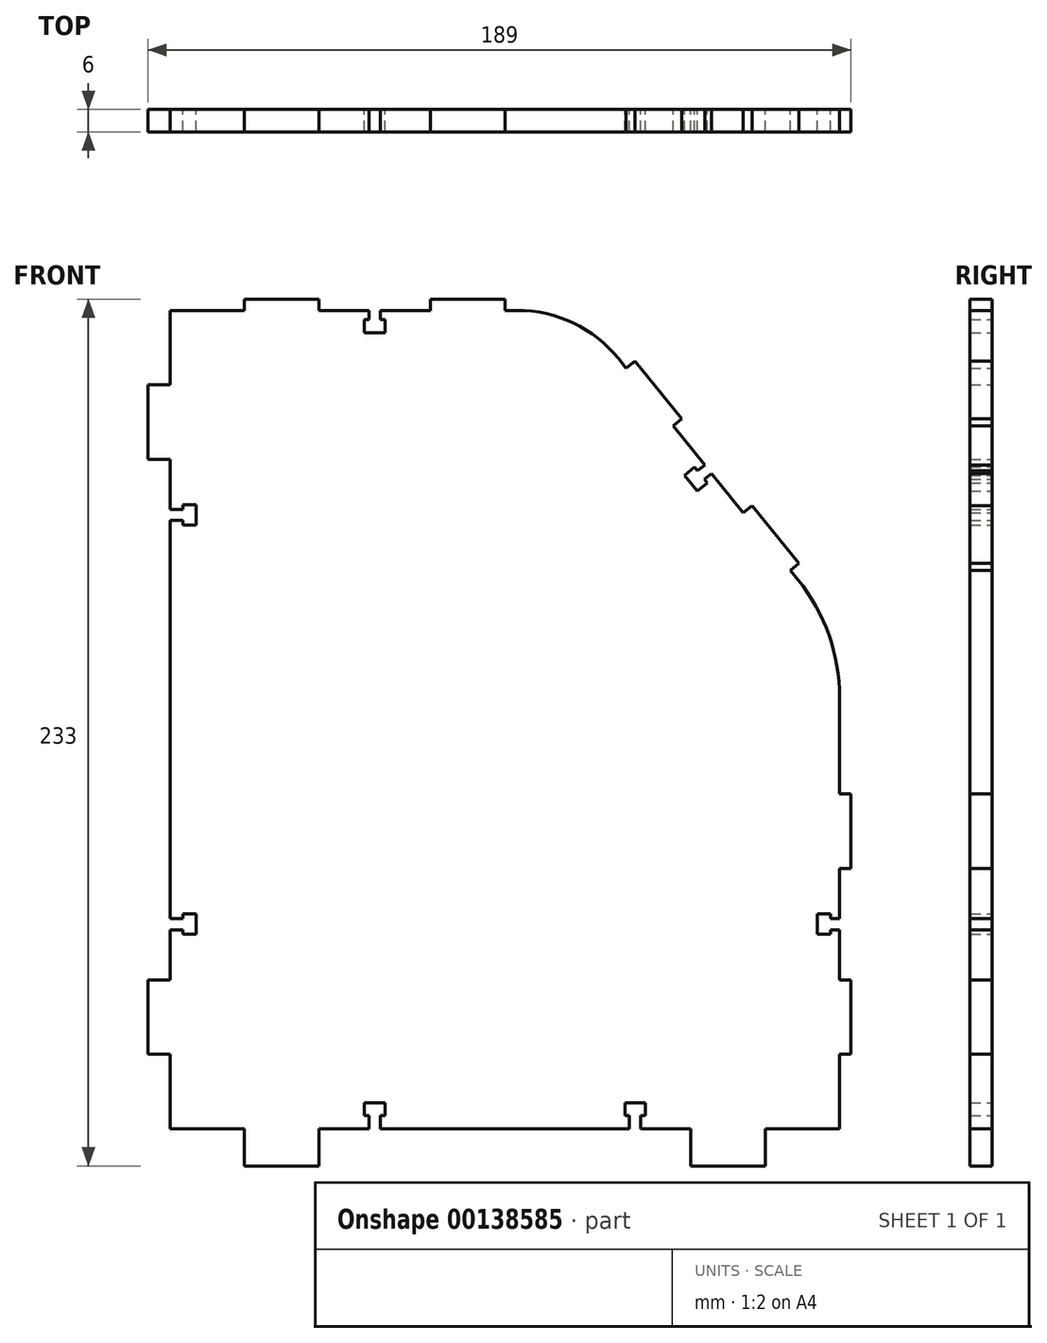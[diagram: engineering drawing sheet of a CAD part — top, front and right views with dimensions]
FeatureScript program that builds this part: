
annotation { "Feature Type Name" : "Feature", "Feature Type Description" : "" }
export const myFeature = defineFeature(function(context is Context, id is Id, definition is map)
    precondition{}
    {
        {
            var Q0;
            Q0=qCreatedBy(makeId("Front.planeOp"),FACE);
            var sketch = newSketch(context, id + "F0", { "sketchPlane" : qUnion([Q0])});
            skLineSegment(sketch, "E0", {"start": v(0, 220) * mm, "end": v(20, 220) * mm});
            skLineSegment(sketch, "E1", {"start": v(20, 220) * mm, "end": v(20, 223) * mm});
            skLineSegment(sketch, "E2", {"start": v(20, 223) * mm, "end": v(40, 223) * mm});
            skLineSegment(sketch, "E3", {"start": v(40, 223) * mm, "end": v(40, 220) * mm});
            skLineSegment(sketch, "E4", {"start": v(40, 220) * mm, "end": v(53.5, 220) * mm});
            skLineSegment(sketch, "E5", {"start": v(53.5, 220) * mm, "end": v(53.5, 217.5) * mm});
            skLineSegment(sketch, "E6", {"start": v(53.5, 217.5) * mm, "end": v(52.25, 217.5) * mm});
            skLineSegment(sketch, "E7", {"start": v(52.25, 217.5) * mm, "end": v(52.25, 214) * mm});
            skLineSegment(sketch, "E8", {"start": v(52.25, 214) * mm, "end": v(57.75, 214) * mm});
            skLineSegment(sketch, "E9", {"start": v(57.75, 214) * mm, "end": v(57.75, 217.5) * mm});
            skLineSegment(sketch, "E10", {"start": v(57.75, 217.5) * mm, "end": v(56.5, 217.5) * mm});
            skLineSegment(sketch, "E11", {"start": v(56.5, 217.5) * mm, "end": v(56.5, 220) * mm});
            skLineSegment(sketch, "E12", {"start": v(56.5, 220) * mm, "end": v(70, 220) * mm});
            skLineSegment(sketch, "E13", {"start": v(70, 220) * mm, "end": v(70, 223) * mm});
            skLineSegment(sketch, "E14", {"start": v(70, 223) * mm, "end": v(90, 223) * mm});
            skLineSegment(sketch, "E15", {"start": v(90, 223) * mm, "end": v(90, 220) * mm});
            skLineSegment(sketch, "E16", {"start": v(90, 220) * mm, "end": v(93.33, 220) * mm});
            skLineSegment(sketch, "E17", {"start": v(0, 200) * mm, "end": v(-6, 200) * mm});
            skLineSegment(sketch, "E18", {"start": v(-6, 200) * mm, "end": v(-6, 180) * mm});
            skLineSegment(sketch, "E19", {"start": v(-6, 180) * mm, "end": v(0, 180) * mm});
            skLineSegment(sketch, "E20", {"start": v(0, 166.5) * mm, "end": v(3.5, 166.5) * mm});
            skLineSegment(sketch, "E21", {"start": v(3.5, 166.5) * mm, "end": v(3.5, 167.75) * mm});
            skLineSegment(sketch, "E22", {"start": v(3.5, 167.75) * mm, "end": v(7, 167.75) * mm});
            skLineSegment(sketch, "E23", {"start": v(7, 167.75) * mm, "end": v(7, 162.25) * mm});
            skLineSegment(sketch, "E24", {"start": v(7, 162.25) * mm, "end": v(3.5, 162.25) * mm});
            skLineSegment(sketch, "E25", {"start": v(3.5, 162.25) * mm, "end": v(3.5, 163.5) * mm});
            skLineSegment(sketch, "E26", {"start": v(3.5, 163.5) * mm, "end": v(0, 163.5) * mm});
            skLineSegment(sketch, "E27", {"start": v(0, 166.5) * mm, "end": v(0, 180) * mm});
            skLineSegment(sketch, "E28", {"start": v(-6, 180) * mm, "end": v(-6, 200) * mm});
            skLineSegment(sketch, "E29", {"start": v(0, 200) * mm, "end": v(0, 220) * mm});
            skPoint(sketch, "E30.visualSharp", {"position": v(110, 220) * mm});
            skArc(sketch, "E30.filletArc", {"start": v(120.5, 207.06) * mm, "mid": v(108.38, 216.6) * mm, "end": v(93.33, 220) * mm});
            skPoint(sketch, "E31.visualSharp", {"position": v(180, 135.15) * mm});
            skArc(sketch, "E31.filletArc", {"start": v(180, 116.03) * mm, "mid": v(177.12, 132.74) * mm, "end": v(168.82, 147.54) * mm});
            skLineSegment(sketch, "E32", {"start": v(0, 163.5) * mm, "end": v(0, 110) * mm});
            skLineSegment(sketch, "E33.MirrorCS", {"start": v(0, 0) * mm, "end": v(0, 0) * mm});
            skLineSegment(sketch, "E34", {"start": v(93.33, 185) * mm, "end": v(110, 220.02) * mm});
            skLineSegment(sketch, "E35", {"start": v(0, 110) * mm, "end": v(180, 110) * mm, "construction": true});
            skLineSegment(sketch, "E36.MirrorCS", {"start": v(0, 56.5) * mm, "end": v(0, 110) * mm});
            skLineSegment(sketch, "E37.MirrorCS", {"start": v(3.5, 57.75) * mm, "end": v(3.5, 56.5) * mm});
            skLineSegment(sketch, "E38.MirrorCS", {"start": v(3.5, 53.5) * mm, "end": v(3.5, 52.25) * mm});
            skLineSegment(sketch, "E39.MirrorCS", {"start": v(-6, 40) * mm, "end": v(0, 40) * mm});
            skLineSegment(sketch, "E40.MirrorCS", {"start": v(0, 20) * mm, "end": v(-6, 20) * mm});
            skLineSegment(sketch, "E41.MirrorCS", {"start": v(7, 52.25) * mm, "end": v(7, 57.75) * mm});
            skLineSegment(sketch, "E42.MirrorCS", {"start": v(7, 57.75) * mm, "end": v(3.5, 57.75) * mm});
            skLineSegment(sketch, "E43.MirrorCS", {"start": v(3.5, 52.25) * mm, "end": v(7, 52.25) * mm});
            skLineSegment(sketch, "E44.MirrorCS", {"start": v(3.5, 56.5) * mm, "end": v(0, 56.5) * mm});
            skLineSegment(sketch, "E45.MirrorCS", {"start": v(-6, 20) * mm, "end": v(-6, 40) * mm});
            skLineSegment(sketch, "E46.MirrorCS", {"start": v(0, 53.5) * mm, "end": v(0, 40) * mm});
            skLineSegment(sketch, "E47.MirrorCS", {"start": v(-6, 40) * mm, "end": v(-6, 20) * mm});
            skLineSegment(sketch, "E48.MirrorCS", {"start": v(0, 20) * mm, "end": v(0, 0) * mm});
            skLineSegment(sketch, "E49.MirrorCS", {"start": v(0, 53.5) * mm, "end": v(3.5, 53.5) * mm});
            skLineSegment(sketch, "E50.MirrorCS", {"start": v(143.67, 174.56) * mm, "end": v(144.45, 173.59) * mm});
            skLineSegment(sketch, "E51.MirrorCS", {"start": v(140.99, 177.86) * mm, "end": v(141.78, 176.89) * mm});
            skLineSegment(sketch, "E52.MirrorCS", {"start": v(156.45, 167.54) * mm, "end": v(154.12, 165.65) * mm});
            skLineSegment(sketch, "E53.MirrorCS", {"start": v(124.93, 206.36) * mm, "end": v(122.6, 204.47) * mm});
            skLineSegment(sketch, "E54.MirrorCS", {"start": v(144.45, 173.59) * mm, "end": v(141.74, 171.38) * mm});
            skLineSegment(sketch, "E55.MirrorCS", {"start": v(122.6, 204.47) * mm, "end": v(120.5, 207.06) * mm});
            skLineSegment(sketch, "E56.MirrorCS", {"start": v(135.2, 188.94) * mm, "end": v(137.54, 190.83) * mm});
            skLineSegment(sketch, "E57.MirrorCS", {"start": v(166.72, 150.12) * mm, "end": v(169.05, 152.01) * mm});
            skLineSegment(sketch, "E58.MirrorCS", {"start": v(138.27, 175.65) * mm, "end": v(140.99, 177.86) * mm});
            skLineSegment(sketch, "E59.MirrorCS", {"start": v(141.78, 176.89) * mm, "end": v(143.72, 178.46) * mm});
            skLineSegment(sketch, "E60.MirrorCS", {"start": v(143.72, 178.46) * mm, "end": v(135.2, 188.94) * mm});
            skLineSegment(sketch, "E61.MirrorCS", {"start": v(145.6, 176.13) * mm, "end": v(143.67, 174.56) * mm});
            skLineSegment(sketch, "E62.MirrorCS", {"start": v(137.54, 190.83) * mm, "end": v(124.93, 206.36) * mm});
            skLineSegment(sketch, "E63.MirrorCS", {"start": v(169.05, 152.01) * mm, "end": v(156.45, 167.54) * mm});
            skLineSegment(sketch, "E64.MirrorCS", {"start": v(154.12, 165.65) * mm, "end": v(145.6, 176.13) * mm});
            skLineSegment(sketch, "E65.MirrorCS", {"start": v(141.74, 171.38) * mm, "end": v(138.27, 175.65) * mm});
            skLineSegment(sketch, "E66", {"start": v(166.72, 150.12) * mm, "end": v(168.82, 147.54) * mm});
            skLineSegment(sketch, "E67", {"start": v(180, 116.03) * mm, "end": v(180, 110) * mm});
            skLineSegment(sketch, "E68", {"start": v(180, 110) * mm, "end": v(180, 90) * mm});
            skLineSegment(sketch, "E69", {"start": v(180, 90) * mm, "end": v(183, 90) * mm});
            skLineSegment(sketch, "E70", {"start": v(183, 90) * mm, "end": v(183, 70) * mm});
            skLineSegment(sketch, "E71", {"start": v(183, 70) * mm, "end": v(180, 70) * mm});
            skLineSegment(sketch, "E72", {"start": v(180, 70) * mm, "end": v(180, 56.5) * mm});
            skLineSegment(sketch, "E73", {"start": v(180, 56.5) * mm, "end": v(177.5, 56.5) * mm});
            skLineSegment(sketch, "E74", {"start": v(177.5, 56.5) * mm, "end": v(177.5, 57.75) * mm});
            skLineSegment(sketch, "E75", {"start": v(177.5, 57.75) * mm, "end": v(174, 57.75) * mm});
            skLineSegment(sketch, "E76", {"start": v(174, 57.75) * mm, "end": v(174, 52.25) * mm});
            skLineSegment(sketch, "E77", {"start": v(174, 52.25) * mm, "end": v(177.5, 52.25) * mm});
            skLineSegment(sketch, "E78", {"start": v(177.5, 52.25) * mm, "end": v(177.5, 53.5) * mm});
            skLineSegment(sketch, "E79", {"start": v(177.5, 53.5) * mm, "end": v(180, 53.5) * mm});
            skLineSegment(sketch, "E80", {"start": v(180, 53.5) * mm, "end": v(180, 40) * mm});
            skLineSegment(sketch, "E81", {"start": v(180, 40) * mm, "end": v(183, 40) * mm});
            skLineSegment(sketch, "E82", {"start": v(183, 40) * mm, "end": v(183, 20) * mm});
            skLineSegment(sketch, "E83", {"start": v(183, 20) * mm, "end": v(180, 20) * mm});
            skLineSegment(sketch, "E84", {"start": v(180, 20) * mm, "end": v(180, 0) * mm});
            skLineSegment(sketch, "E85.MirrorCS", {"start": v(20, 0) * mm, "end": v(20, -10) * mm});
            skLineSegment(sketch, "E86.MirrorCS", {"start": v(40, -10) * mm, "end": v(40, 0) * mm});
            skLineSegment(sketch, "E87.MirrorCS", {"start": v(20, -10) * mm, "end": v(40, -10) * mm});
            skLineSegment(sketch, "E88", {"start": v(90, 0) * mm, "end": v(90, 110) * mm, "construction": true});
            skLineSegment(sketch, "E89.MirrorCS", {"start": v(160, -10) * mm, "end": v(140, -10) * mm});
            skLineSegment(sketch, "E90.MirrorCS", {"start": v(160, 0) * mm, "end": v(160, -10) * mm});
            skLineSegment(sketch, "E91", {"start": v(0, 0) * mm, "end": v(20, 0) * mm});
            skLineSegment(sketch, "E92", {"start": v(160, 0) * mm, "end": v(180, 0) * mm});
            skLineSegment(sketch, "E93", {"start": v(40, 220) * mm, "end": v(70, 220) * mm, "construction": true});
            skLineSegment(sketch, "E94", {"start": v(55, 220) * mm, "end": v(55, 212.29) * mm, "construction": true});
            skPoint(sketch, "E95", {"position": v(55, 214) * mm});
            skLineSegment(sketch, "E96", {"start": v(7, 165) * mm, "end": v(-15.94, 165) * mm, "construction": true});
            skLineSegment(sketch, "E97", {"start": v(174, 55) * mm, "end": v(193.5, 55) * mm, "construction": true});
            skLineSegment(sketch, "E98.MirrorCS", {"start": v(55, 0) * mm, "end": v(55, 7.71) * mm, "construction": true});
            skLineSegment(sketch, "E99", {"start": v(40, 0) * mm, "end": v(53.5, 0) * mm});
            skLineSegment(sketch, "E100", {"start": v(53.5, 0) * mm, "end": v(53.5, 3.5) * mm});
            skLineSegment(sketch, "E101", {"start": v(53.5, 3.5) * mm, "end": v(52.25, 3.5) * mm});
            skLineSegment(sketch, "E102", {"start": v(52.25, 3.5) * mm, "end": v(52.25, 7) * mm});
            skLineSegment(sketch, "E103", {"start": v(52.25, 7) * mm, "end": v(57.75, 7) * mm});
            skLineSegment(sketch, "E104", {"start": v(57.75, 7) * mm, "end": v(57.75, 3.5) * mm});
            skLineSegment(sketch, "E105", {"start": v(57.75, 3.5) * mm, "end": v(56.5, 3.5) * mm});
            skLineSegment(sketch, "E106", {"start": v(56.5, 3.5) * mm, "end": v(56.5, 0) * mm});
            skLineSegment(sketch, "E107", {"start": v(56.5, 0) * mm, "end": v(90, 0) * mm});
            skPoint(sketch, "E108", {"position": v(55, 7) * mm});
            skLineSegment(sketch, "E109.MirrorCS", {"start": v(127.75, 3.5) * mm, "end": v(127.75, 7) * mm});
            skLineSegment(sketch, "E110.MirrorCS", {"start": v(122.25, 7) * mm, "end": v(122.25, 3.5) * mm});
            skLineSegment(sketch, "E111.MirrorCS", {"start": v(122.25, 3.5) * mm, "end": v(123.5, 3.5) * mm});
            skLineSegment(sketch, "E112.MirrorCS", {"start": v(126.5, 3.5) * mm, "end": v(127.75, 3.5) * mm});
            skLineSegment(sketch, "E113.MirrorCS", {"start": v(127.75, 7) * mm, "end": v(122.25, 7) * mm});
            skLineSegment(sketch, "E114.MirrorCS", {"start": v(125, 0) * mm, "end": v(125, 7.71) * mm, "construction": true});
            skPoint(sketch, "E115.MirrorP", {"position": v(125, 7) * mm});
            skLineSegment(sketch, "E116.MirrorCS", {"start": v(140, 0) * mm, "end": v(126.5, 0) * mm});
            skLineSegment(sketch, "E117.MirrorCS", {"start": v(140, -10) * mm, "end": v(140, 0) * mm});
            skLineSegment(sketch, "E118.MirrorCS", {"start": v(123.5, 3.5) * mm, "end": v(123.5, 0) * mm});
            skLineSegment(sketch, "E119.MirrorCS", {"start": v(126.5, 0) * mm, "end": v(126.5, 3.5) * mm});
            skLineSegment(sketch, "E120.MirrorCS", {"start": v(123.5, 0) * mm, "end": v(90, 0) * mm});
            skSolve(sketch);
        }
        {
            var Q0;
            Q0=makeQuery(id+"F0.imprint","IMPRINT",FACE,{"disambiguationData":[TD([[makeQuery(id+"F0.imprint","IMPRINT",EDGE,{"derivedFrom":sQuery(id+"F0.wireOp",EDGE,"E0")}),-1.0]])]});
            var Q1;
            Q1=makeQuery(id+"F0.imprint","IMPRINT",FACE,{"disambiguationData":[TD([[makeQuery(id+"F0.imprint","IMPRINT",EDGE,{"derivedFrom":sQuery(id+"F0.wireOp",EDGE,"7zwvuXE3-DbRT-44SM-j9et-4jxJWr9VXILD")}),-1.0]])]});
            extrude(context, id + "F1", {"entities" : qUnion([Q0, Q1]), "depth" : 6 * mm});
        }
    });
